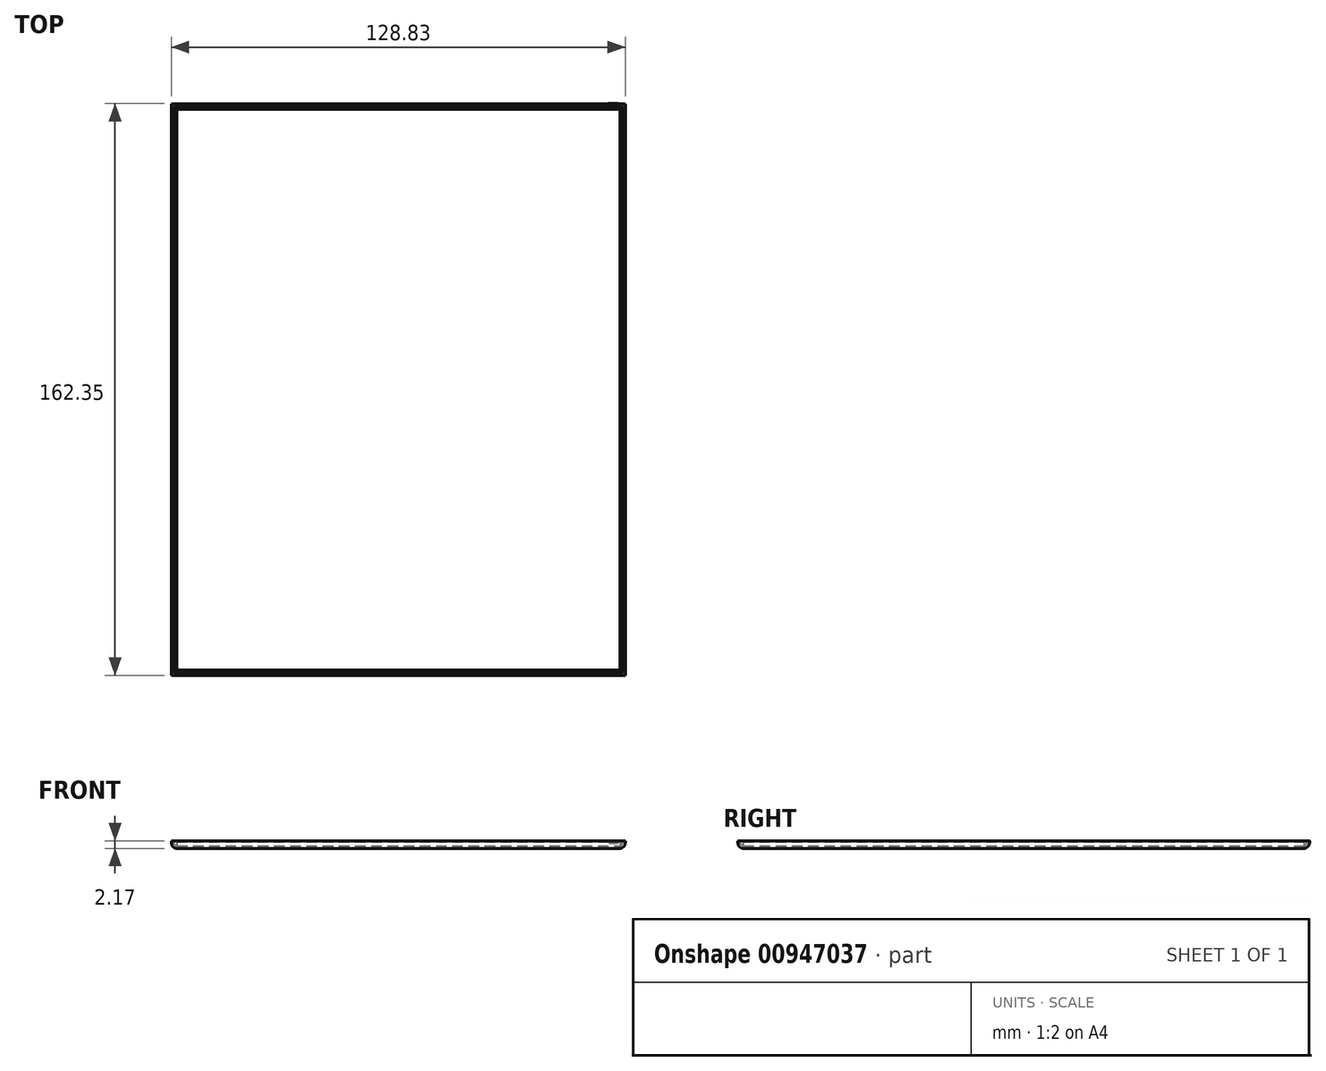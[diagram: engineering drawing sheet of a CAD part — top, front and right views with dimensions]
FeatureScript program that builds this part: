
annotation { "Feature Type Name" : "Feature", "Feature Type Description" : "" }
export const myFeature = defineFeature(function(context is Context, id is Id, definition is map)
    precondition{}
    {
        {
            var Q0;
            Q0=qCreatedBy(makeId("Top.planeOp"),FACE);
            var sketch = newSketch(context, id + "F0", { "sketchPlane" : qUnion([Q0])});
            skLineSegment(sketch, "E0.bottom", {"start": v(-64.31, 65.35) * mm, "end": v(64.52, 65.35) * mm});
            skLineSegment(sketch, "E0.top", {"start": v(-64.31, -96.88) * mm, "end": v(64.52, -96.88) * mm});
            skLineSegment(sketch, "E0.left", {"start": v(-64.31, 65.35) * mm, "end": v(-64.31, -96.88) * mm});
            skLineSegment(sketch, "E0.right", {"start": v(64.52, 65.35) * mm, "end": v(64.52, -96.88) * mm});
            skSolve(sketch);
        }
        {
            var Q0;
            Q0=makeQuery(id+"F0.imprint","IMPRINT",FACE,{"disambiguationData":[TD([[makeQuery(id+"F0.imprint","IMPRINT",EDGE,{"derivedFrom":sQuery(id+"F0.wireOp",EDGE,"E0.bottom")}),-1.0]])]});
            extrude(context, id + "F1", {"entities" : qUnion([Q0]), "oppositeDirection" : true, "depth" : 2.17 * mm, "offsetDistance" : 25.4 * mm});
        }
        {
            var Q0;
            Q0=makeQuery(id+"F1.opExtrude","CAP_FACE",FACE,{"disambiguationData":[OSD([sQuery(id+"F0.wireOp",EDGE,"E0.bottom"),sQuery(id+"F0.wireOp",EDGE,"E0.top"),sQuery(id+"F0.wireOp",EDGE,"E0.left"),sQuery(id+"F0.wireOp",EDGE,"E0.right")])],"isStart":false});
            fillet(context, id + "F2", {"entities" : qUnion([Q0]), "radius" : 1.52 * mm, "tangentPropagation" : true, "allowEdgeOverflow" : false});
        }
        {
            var Q0;
            Q0=makeQuery(id+"F1.opExtrude","CAP_FACE",FACE,{"disambiguationData":[OSD([sQuery(id+"F0.wireOp",EDGE,"E0.bottom"),sQuery(id+"F0.wireOp",EDGE,"E0.top"),sQuery(id+"F0.wireOp",EDGE,"E0.left"),sQuery(id+"F0.wireOp",EDGE,"E0.right")])],"isStart":true});
            var sketch = newSketch(context, id + "F3", { "sketchPlane" : qUnion([Q0])});
            skCircle(sketch, "E1", {"center": v(0, -88.4) * mm, "radius": 4.4 * mm});
            skSolve(sketch);
        }
        {
            var Q0;
            Q0=sQuery(id+"F3.wireOp",EDGE,"E1");
            extrude(context, id + "F4", {"bodyType" : ToolBodyType.SURFACE, "surfaceEntities" : qUnion([Q0]), "oppositeDirection" : true, "depth" : 1.7 * mm, "offsetDistance" : 25.4 * mm});
        }
        {
            var Q0;
            Q0=makeQuery(id+"F1.opExtrude","CAP_FACE",FACE,{"disambiguationData":[OSD([sQuery(id+"F0.wireOp",EDGE,"E0.bottom"),sQuery(id+"F0.wireOp",EDGE,"E0.top"),sQuery(id+"F0.wireOp",EDGE,"E0.left"),sQuery(id+"F0.wireOp",EDGE,"E0.right")])],"isStart":true});
            shell(context, id + "F5", {"entities" : qUnion([Q0]), "thickness" : 0.76 * mm});
        }
        {
            var Q0;
            Q0=makeQuery(id+"F5.opShell","OFFSET_FACE",FACE,{"disambiguationData":[OSD([sQuery(id+"F0.wireOp",EDGE,"E0.bottom"),sQuery(id+"F0.wireOp",EDGE,"E0.top"),sQuery(id+"F0.wireOp",EDGE,"E0.left"),sQuery(id+"F0.wireOp",EDGE,"E0.right")])]});
            var sketch = newSketch(context, id + "F6", { "sketchPlane" : qUnion([Q0])});
            skLineSegment(sketch, "E2.bottom", {"start": v(-62.79, 63.82) * mm, "end": v(63, 63.82) * mm});
            skLineSegment(sketch, "E2.top", {"start": v(-62.79, -95.36) * mm, "end": v(63, -95.36) * mm});
            skLineSegment(sketch, "E2.left", {"start": v(-62.79, 63.82) * mm, "end": v(-62.79, -95.36) * mm});
            skLineSegment(sketch, "E2.right", {"start": v(63, 63.82) * mm, "end": v(63, -95.36) * mm});
            skSolve(sketch);
        }
        {
            var Q0;
            Q0=makeQuery(id+"F6.imprint","IMPRINT",FACE,{"disambiguationData":[TD([[makeQuery(id+"F6.imprint","IMPRINT",EDGE,{"derivedFrom":sQuery(id+"F6.wireOp",EDGE,"E2.bottom")}),-1.0]])]});
            extrude(context, id + "F7", {"entities" : qUnion([Q0]), "operationType" : NewBodyOperationType.ADD, "depth" : 1.12 * mm, "offsetDistance" : 25.4 * mm});
        }
        {
            var Q0;
            Q0=makeQuery(id+"F1.opExtrude","SWEPT_FACE",FACE,{"disambiguationData":[OSD([sQuery(id+"F0.wireOp",EDGE,"E0.bottom")])]});
            var sketch = newSketch(context, id + "F8", { "sketchPlane" : qUnion([Q0])});
            skLineSegment(sketch, "E3.bottom", {"start": v(-62.27, 0) * mm, "end": v(-60.07, 0) * mm});
            skLineSegment(sketch, "E3.top", {"start": v(-62.27, -0.65) * mm, "end": v(-60.07, -0.65) * mm});
            skLineSegment(sketch, "E3.left", {"start": v(-62.27, 0) * mm, "end": v(-62.27, -0.65) * mm});
            skLineSegment(sketch, "E3.right", {"start": v(-60.07, 0) * mm, "end": v(-60.07, -0.65) * mm});
            skSolve(sketch);
        }
        {
            var Q0;
            Q0=makeQuery(id+"F8.imprint","IMPRINT",FACE,{"disambiguationData":[TD([[makeQuery(id+"F8.imprint","IMPRINT",EDGE,{"derivedFrom":sQuery(id+"F8.wireOp",EDGE,"E3.bottom")}),1.0]])]});
            var sketch = newSketch(context, id + "F9", { "sketchPlane" : qUnion([Q0])});
            skCircle(sketch, "E4", {"center": v(-60.07, -0.3) * mm, "radius": 0.3 * mm});
            skSolve(sketch);
        }
        {
            var Q0;
            {var subQ1=makeQuery(id+"F8.imprint","IMPRINT",EDGE,{"derivedFrom":sQuery(id+"F8.wireOp",EDGE,"E3.bottom")});Q0=makeQuery(id+"F9.imprint","IMPRINT",FACE,{"disambiguationData":[TD([[makeQuery(id+"F9.imprint","IMPRINT",EDGE,{"derivedFrom":subQ1}),1.0]])]});}
            var sketch = newSketch(context, id + "F10", { "sketchPlane" : qUnion([Q0])});
            skCircle(sketch, "E5", {"center": v(-62.27, -0.31) * mm, "radius": 0.32 * mm});
            skSolve(sketch);
        }
        {
            var Q0;
            Q0=makeQuery(id+"F8.imprint","IMPRINT",FACE,{"disambiguationData":[TD([[makeQuery(id+"F8.imprint","IMPRINT",EDGE,{"derivedFrom":sQuery(id+"F8.wireOp",EDGE,"E3.bottom")}),1.0]])]});
            var Q1;
            Q1 = qSketchRegion(id + "F10", true);
            var Q2;
            Q2 = qSketchRegion(id + "F9", true);
            extrude(context, id + "F11", {"entities" : qUnion([Q0, Q1, Q2]), "operationType" : NewBodyOperationType.ADD, "depth" : 0.12 * mm, "offsetDistance" : 25.4 * mm});
        }
    });
